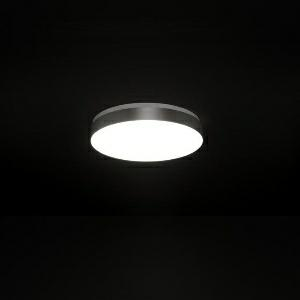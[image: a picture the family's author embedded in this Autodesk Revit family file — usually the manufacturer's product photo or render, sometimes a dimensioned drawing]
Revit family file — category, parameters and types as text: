
# Revit family: spectral_norea_norea-rp_306_1900_840_mps_7a2f
name_source: partatom
category: Lighting Fixtures
revit_build: Autodesk Revit 2016 (Build: 20150220_1215(x64)
units: mm (PartAtom-declared; Revit-internal decimal feet)

## family parameters
Cut with Voids When Loaded = No
Host = Face
Light Source = No
Part Type = Normal
Room Calculation Point = No
Round Connector Dimension = Use Diameter
Shared = No

## types (1)
- SPECTRAL NOREA (1 x )
    Apparent Load = 0 VA
    Approval mark = CE
    CIE Flux Codes = 73 93 98 100 62
    Control Gear = Electronic transformer
    Default Elevation = 1800 mm
    Description = SPT0000130
NOREA Pendant luminaire

Design:
Round luminaire element with a microprism panel in a natural anodised aluminium profile frame surround. The frame is fixed at the powder-coated metal body by a bayonet fixture with spring clip. The luminaire is suspended by a six trapezoidal wire pendants with ceiling fixture and transparent connecting cable round ceiling junction box. Cable length adjustable at the junction box, steel wire steplessly height adjustable. The metal body accommodates the electrical components and electronic ballast. The LED module is formed as a round LED flat board and can be removed for mounting or exchange using a keyhole screw connection. Plug-in electrical connection of the LED flat board. Luminaire with heat-resistant wiring. Variant suitable for office use with a microprism panel MPS. The LED points are visible as circles on the microprism panel. Also in a dimmable version.
Protection rating IP20, safety class I.

Colour:
Housing – similar to RAL 9016 White silk matt;
Frame – natural anodised
    Height = 78 mm  [stored 0.255906 ft]
    Lamp = 1 x
    Lamp count = 1
    Length = 306 mm
    Luminous efficacy = 0 lm/W
    Manufacturer = Ridi
    ModVariant = No
    Model = NOREA-RP 306/1900/840 MPS
    Mounting Place = Ceiling
    Mounting Type = Pendant
    Number of Poles = 1
    OnlyDefault = Yes
    Power Factor = 1
    Product Name = SPECTRAL NOREA
    Product group = Pendant luminaire
    ProductGroupID = 9
    Protection Class = Protection class
    Protection Degree = IP 20
    RlxData = <blob elided: 30341 chars, md5=2f50f5e1>
    Socket = socket
    Standby Power = 0 W
    System Light Flux = 0 lm
    System Power = 0 W
    Type Image = rundmittel01_-_kopie.jpg
    URL = http://reluxnet.relux.com
    VarID = 1
    Voltage = 0 V
    Weight = 0.00 kg
    Width = 0 mm  [stored 0 ft]

note: [stored X ft] marks values corroborated as IEEE doubles in the binary element streams (Revit-internal decimal feet)

## geometry (parser evidence)
native form markers: Sweep x11
no freeform markers — native parametric forms only
